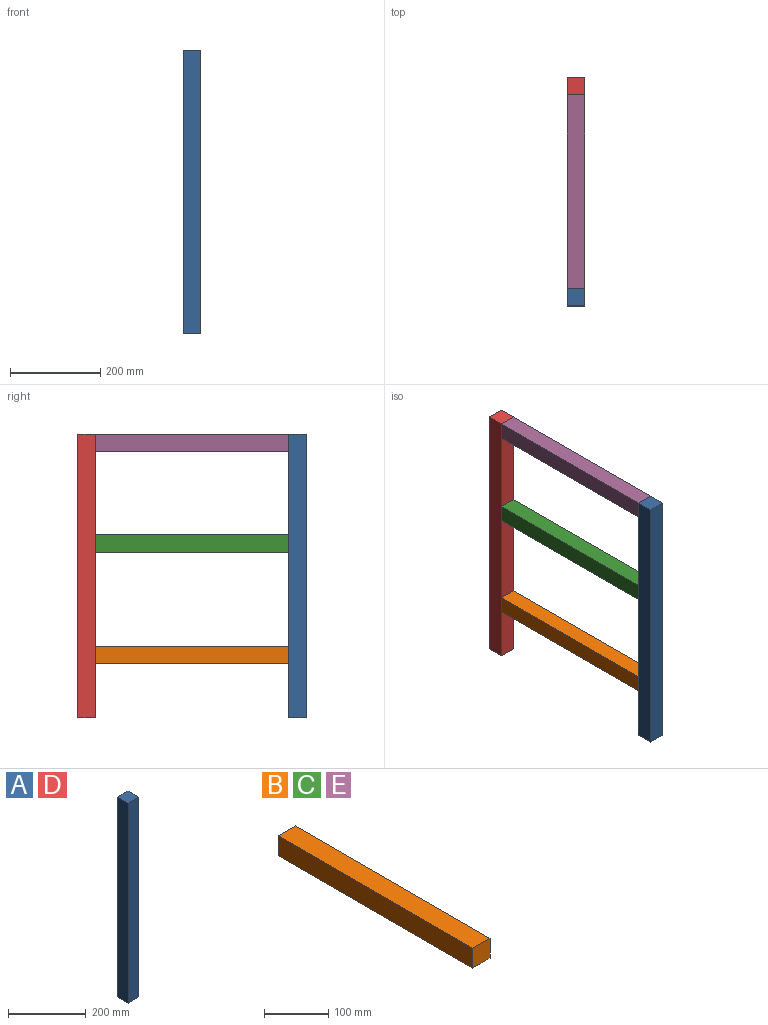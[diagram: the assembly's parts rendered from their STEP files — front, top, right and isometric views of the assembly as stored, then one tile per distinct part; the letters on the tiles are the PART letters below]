
ASSEMBLY  parts=5 mates=4
PART A: 6 faces, bbox 38x38x630 mm
  f0: plane 38x38mm, normal (0,0,1), area 1444mm2, adj f1,f3,f4,f5
  f1: plane 630x38mm, normal (-1,0,0), area 23940mm2, adj f0,f2,f4,f5
  f2: plane 38x38mm, normal (0,0,-1), area 1444mm2, adj f1,f3,f4,f5
  f3: plane 630x38mm, normal (1,0,0), area 23940mm2, adj f0,f2,f4,f5
  f4: plane 630x38mm, normal (0,-1,0), area 23940mm2, adj f0,f1,f2,f3
  f5: plane 630x38mm, normal (0,1,0), area 23940mm2, adj f0,f1,f2,f3
PART B: 6 faces, bbox 38x430x38 mm
  f0: plane 430x38mm, normal (0,0,1), area 16340mm2, adj f1,f3,f4,f5
  f1: plane 38x38mm, normal (0,-1,0), area 1444mm2, adj f0,f2,f4,f5
  f2: plane 430x38mm, normal (0,0,-1), area 16340mm2, adj f1,f3,f4,f5
  f3: plane 38x38mm, normal (0,1,0), area 1444mm2, adj f0,f2,f4,f5
  f4: plane 430x38mm, normal (1,0,0), area 16340mm2, adj f0,f1,f2,f3
  f5: plane 430x38mm, normal (-1,0,0), area 16340mm2, adj f0,f1,f2,f3
PART C: same geometry as B
PART D: same geometry as A
PART E: same geometry as B
PLACE A t=(-135.78,-73.93,94.64)mm
PLACE B t=(-173.78,356.07,214.64)mm
PLACE C t=(-173.78,356.07,462.64)mm
PLACE D t=(-135.78,394.07,94.64)mm
PLACE E t=(-173.78,356.07,686.64)mm
MATE fastened B.f1 <-> A.f5  axis (0,-1,0) through (-154.78,-73.93,214.64)mm
MATE fastened D.f4 <-> E.f3  axis (0,-1,0) through (-154.78,356.07,724.64)mm
MATE fastened C.f1 <-> A.f5  axis (0,-1,0) through (-154.78,-73.93,462.64)mm
MATE fastened A.f5 <-> E.f1  axis (0,1,0) through (-154.78,-73.93,724.64)mm
